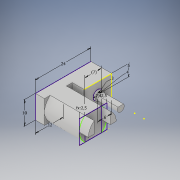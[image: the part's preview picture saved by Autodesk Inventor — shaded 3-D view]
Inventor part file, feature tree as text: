
AUTODESK INVENTOR PART (.ipt)
format: ipt  version: 2019 (Build 230136000, 136)  size: 175,616 bytes
history: native  units: mm
features: extrude x10, sketch x6, other x1
ambient origin geometry x8: Origin, YZ Plane, XZ Plane, XY Plane, X Axis, Y Axis, Z Axis, Center Point
bodies: Solid1 (feature_tree)
feature tree (17):
  sketch  "Sketch1"  dims[d0=24.0mm d1=10.0mm]
  extrude  "Extrusion1"  Depth=10.0mm
  extrude  "Extrusion2"  Depth=19.0mm TaperAngle=0.0deg
  sketch  "Sketch2"  dims[d2=12.0mm d3=19.0mm d4=0.0mm]
  extrude  "Extrusion3"  Depth=4.0mm
  extrude  "Extrusion4"  Depth=6.0mm
  extrude  "Extrusion5"  Depth=2.4mm
  sketch  "Sketch3"  dims[d5=9.0mm d6=0.0mm d7=4.0mm]
  extrude  "Extrusion6"  Depth=10.0mm TaperAngle=0.0deg
  extrude  "Extrusion7"  Depth=1.0mm TaperAngle=0.0deg
  extrude  "Extrusion8"  Depth=2.5mm
  extrude  "Extrusion9"  Depth=2.5mm
  other  "Work Axis1"
  sketch  "Sketch5"  dims[d10=3.0mm d11=2.4mm]
  extrude  "Extrusion10"  Depth=4.0mm
  sketch  "Sketch4"  dims[d8=5.0mm d9=6.0mm]
  sketch  "Sketch6"  dims[d12=1.0mm d13=0.0mm d14=10.0mm d15=0.0mm d16=1.0mm d17=0.0mm d18=2.5mm d19=2.5mm d20=7.0mm d21=15.0mm d22=0.0mm d23=15.0mm d24=0.0mm d25=4.0mm d26=0.0mm d27=4.0mm d28=0.0mm d29=8.0mm d30=0.0mm]
